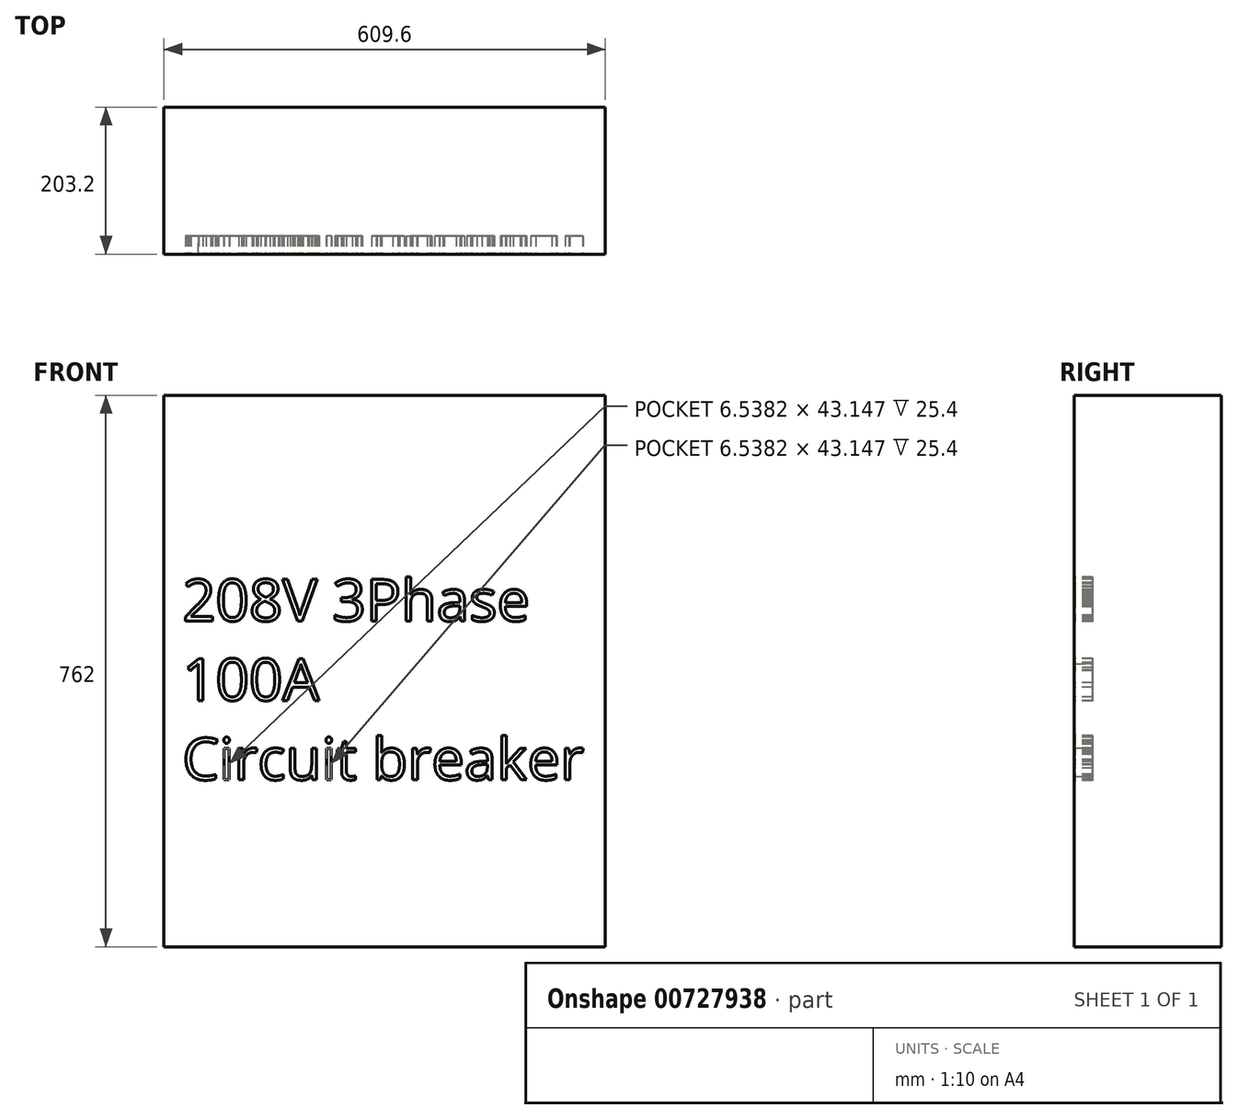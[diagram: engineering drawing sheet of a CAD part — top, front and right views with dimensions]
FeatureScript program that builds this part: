
annotation { "Feature Type Name" : "Feature", "Feature Type Description" : "" }
export const myFeature = defineFeature(function(context is Context, id is Id, definition is map)
    precondition{}
    {
        {
            var Q0;
            Q0=qCreatedBy(makeId("Front.planeOp"),FACE);
            var sketch = newSketch(context, id + "F0", { "sketchPlane" : qUnion([Q0])});
            skLineSegment(sketch, "E0.bottom", {"start": v(304.8, -381) * mm, "end": v(-304.8, -381) * mm});
            skLineSegment(sketch, "E0.top", {"start": v(304.8, 381) * mm, "end": v(-304.8, 381) * mm});
            skLineSegment(sketch, "E0.left", {"start": v(304.8, -381) * mm, "end": v(304.8, 381) * mm});
            skLineSegment(sketch, "E0.right", {"start": v(-304.8, -381) * mm, "end": v(-304.8, 381) * mm});
            skPoint(sketch, "E0.middle", {"position": v(0, 0) * mm});
            skSolve(sketch);
        }
        {
            var Q0;
            Q0 = qSketchRegion(id + "F0", true);
            extrude(context, id + "F1", {"entities" : qUnion([Q0]), "depth" : 203.2 * mm, "offsetDistance" : 25.4 * mm});
        }
        {
            var Q0;
            Q0=makeQuery(id+"F1.opExtrude","CAP_FACE",FACE,{"disambiguationData":[OSD([sQuery(id+"F0.wireOp",EDGE,"E0.bottom"),sQuery(id+"F0.wireOp",EDGE,"E0.top"),sQuery(id+"F0.wireOp",EDGE,"E0.left"),sQuery(id+"F0.wireOp",EDGE,"E0.right")])],"isStart":false});
            var sketch = newSketch(context, id + "F2", { "sketchPlane" : qUnion([Q0])});
            skText(sketch, "E1", { "text": "208V 3Phase\n100A\nCircuit breaker\n", "fontName": "OpenSans-Regular.ttf"});
            const initialGuessF2  = {"E1": [-0.2794, 0.06895, 1, 0, 0.05805]};
            skSetInitialGuess(sketch, initialGuessF2);
            skSolve(sketch);
        }
        {
            var Q0;
            Q0 = qSketchRegion(id + "F2", true);
            extrude(context, id + "F3", {"entities" : qUnion([Q0]), "operationType" : NewBodyOperationType.REMOVE, "oppositeDirection" : true, "depth" : 25.4 * mm, "offsetDistance" : 25.4 * mm});
        }
    });
